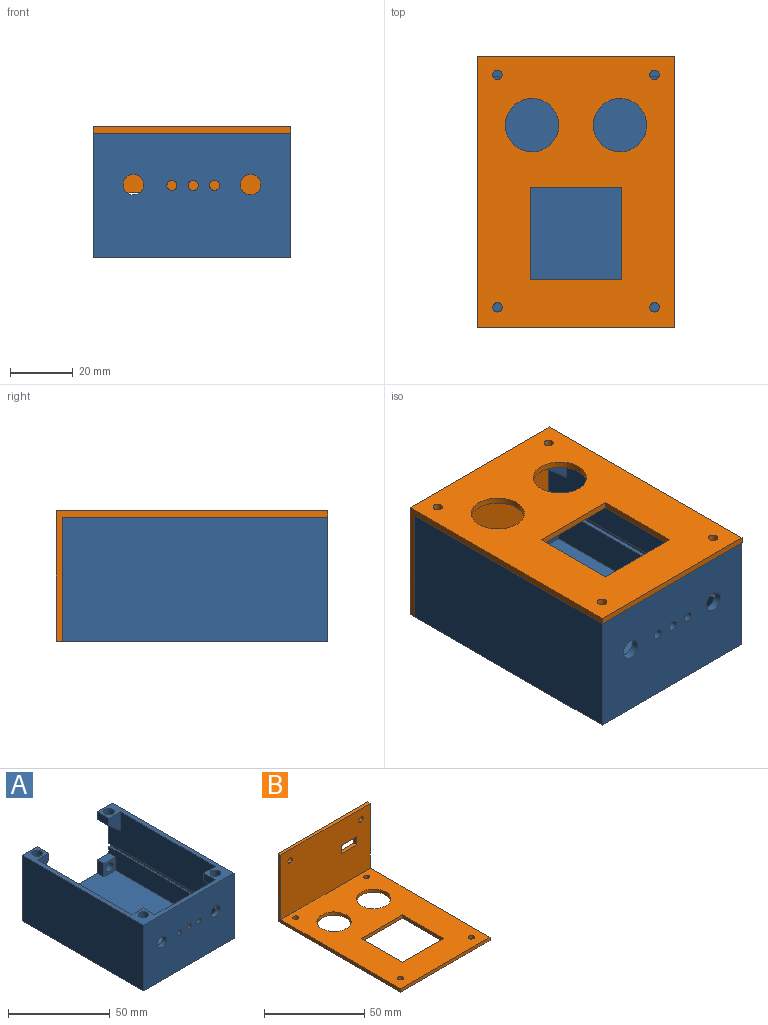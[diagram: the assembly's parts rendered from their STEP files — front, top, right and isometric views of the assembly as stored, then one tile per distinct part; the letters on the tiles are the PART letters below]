
ASSEMBLY  parts=2 mates=1
PART A: 47 faces, bbox 64x85.5x40.5 mm
  f0: plane 60x37mm, normal (0,1,0), area 1931.5mm2, adj f1,f2,f3,f4,f8,f9,f10,f11
  f1: plane 82x23mm, normal (-1,0,0), area 1702mm2, adj f0,f8,f9,f16,f34,f40,f44,f45
  f2: plane 82x23mm, normal (1,0,0), area 1702mm2, adj f0,f4,f8,f16,f32,f37,f43,f46
  f3: plane 82x58mm, normal (0,0,1), area 4684mm2, adj f0,f12,f13,f16,f17,f20,f21,f24
  f4: plane 82x1mm, normal (0,0,-1), area 82mm2, adj f0,f2,f15,f16
  f5: plane 84.5x39.5mm, normal (-1,0,0), area 3337.8mm2, adj f6,f8,f16,f30
  f6: plane 84.5x63mm, normal (0,0,-1), area 5323.5mm2, adj f5,f7,f16,f30
  f7: plane 84.5x39.5mm, normal (1,0,0), area 3337.8mm2, adj f6,f8,f16,f30
  f8: plane 84.5x63mm, normal (0,0,1), area 738.6mm2, adj f0,f1,f2,f5,f7,f16,f30,f31
  f9: plane 82x1mm, normal (0,0,-1), area 82mm2, adj f0,f1,f10,f16
  f10: plane 82x2mm, normal (-1,0,0), area 164mm2, adj f0,f9,f11,f16
  f11: plane 82x1mm, normal (0,0,1), area 82mm2, adj f0,f10,f12,f16
  f12: plane 82x12mm, normal (-1,0,0), area 948mm2, adj f0,f3,f11,f16,f19,f20
  f13: plane 82x12mm, normal (1,0,0), area 948mm2, adj f0,f3,f14,f16,f22,f24
  f14: plane 82x1mm, normal (0,0,1), area 82mm2, adj f0,f13,f15,f16
  f15: plane 82x2mm, normal (1,0,0), area 164mm2, adj f0,f4,f14,f16
  f16: plane 63x39.5mm, normal (0,1,0), area 552mm2, adj f1,f2,f3,f4,f5,f6,f7,f8
  f17: plane 8x4.5mm, normal (-1,0,0), area 36mm2, adj f3,f16,f19,f20
  f18: cylinder r=2.6mm len=5.2mm, axis (0,1,0), area 73.5mm2, adj f16,f20
  f19: plane 8x4.5mm, normal (0,0,1), area 36mm2, adj f12,f16,f17,f20
  f20: plane 8x8mm, normal (0,-1,0), area 42.8mm2, adj f3,f12,f17,f18,f19
  f21: plane 8x4.5mm, normal (1,0,0), area 36mm2, adj f3,f16,f22,f24
  f22: plane 8x4.5mm, normal (0,0,1), area 36mm2, adj f13,f16,f21,f24
  f23: cylinder r=2.6mm len=5.2mm, axis (0,1,0), area 73.5mm2, adj f16,f24
  f24: plane 8x8mm, normal (0,-1,0), area 42.8mm2, adj f3,f13,f21,f22,f23
  f25: cylinder r=3.25mm len=6.5mm, axis (0,1,0), area 51.1mm2, adj f0,f30
  f26: cylinder r=1.6mm len=3.2mm, axis (0,1,0), area 25.1mm2, adj f0,f30
  f27: cylinder r=1.6mm len=3.2mm, axis (0,1,0), area 25.1mm2, adj f0,f30
  f28: cylinder r=1.6mm len=3.2mm, axis (0,1,0), area 25.1mm2, adj f0,f30
  f29: cylinder r=3.25mm len=6.5mm, axis (0,1,0), area 51.1mm2, adj f0,f30
  f30: plane 63x39.5mm, normal (0,-1,0), area 2398mm2, adj f5,f6,f7,f8,f25,f26,f27,f28
  f31: plane 8x4.5mm, normal (1,0,0), area 36mm2, adj f0,f8,f32,f46
  f32: plane 11.5x8mm, normal (0,1,0), area 64mm2, adj f2,f8,f31,f46
  f33: cylinder r=2.6mm len=10.31mm, axis (0,0,1), area 130.7mm2, adj f8,f46
  f34: plane 11.5x8mm, normal (0,1,0), area 64mm2, adj f1,f8,f35,f45
  f35: plane 8x4.5mm, normal (-1,0,0), area 36mm2, adj f0,f8,f34,f45
  f36: cylinder r=2.6mm len=10.28mm, axis (0,0,1), area 130.7mm2, adj f8,f45
  f37: plane 11.5x8mm, normal (0,-1,0), area 64mm2, adj f2,f8,f38,f43
  f38: plane 8x4.5mm, normal (1,0,0), area 36mm2, adj f8,f16,f37,f43
  f39: cylinder r=2.6mm len=10.31mm, axis (0,0,1), area 130.7mm2, adj f8,f43
  f40: plane 11.5x8mm, normal (0,-1,0), area 64mm2, adj f1,f8,f41,f44
  f41: plane 8x4.5mm, normal (-1,0,0), area 36mm2, adj f8,f16,f40,f44
  f42: cylinder r=2.6mm len=10.28mm, axis (0,0,1), area 130.7mm2, adj f8,f44
  f43: plane 8x8mm, normal (0.66,0,-0.75), area 56.8mm2, adj f2,f16,f37,f38,f39
  f44: plane 8.96x8.96mm, normal (-0.66,0,-0.75), area 56.8mm2, adj f1,f16,f40,f41,f42
  f45: plane 8.96x8.96mm, normal (-0.66,0,-0.75), area 56.8mm2, adj f0,f1,f34,f35,f36
  f46: plane 8x8mm, normal (0.66,0,-0.75), area 56.8mm2, adj f0,f2,f31,f32,f33
PART B: 24 faces, bbox 63x86.5x41.5 mm
  f0: plane 63x39.5mm, normal (0,-1,0), area 2419.4mm2, adj f2,f3,f15,f17,f18,f19,f20,f21
  f1: plane 63x41.5mm, normal (0,1,0), area 2545.4mm2, adj f2,f3,f16,f17,f18,f19,f20,f21
  f2: plane 86.5x41.5mm, normal (1,0,0), area 252mm2, adj f0,f1,f14,f15,f16,f17
  f3: plane 86.5x41.5mm, normal (-1,0,0), area 252mm2, adj f0,f1,f14,f15,f16,f17
  f4: plane 29x2mm, normal (-1,0,0), area 58mm2, adj f5,f7,f15,f16
  f5: plane 29x2mm, normal (0,1,0), area 58mm2, adj f4,f6,f15,f16
  f6: plane 29x2mm, normal (1,0,0), area 58mm2, adj f5,f7,f15,f16
  f7: plane 29x2mm, normal (0,-1,0), area 58mm2, adj f4,f6,f15,f16
  f8: cylinder r=1.5mm len=3mm, axis (0,0,-1), area 18.8mm2, adj f15,f16
  f9: cylinder r=1.5mm len=3mm, axis (0,0,-1), area 18.8mm2, adj f15,f16
  f10: cylinder r=8.5mm len=17mm, axis (0,0,-1), area 106.8mm2, adj f15,f16
  f11: cylinder r=8.5mm len=17mm, axis (0,0,-1), area 106.8mm2, adj f15,f16
  f12: cylinder r=1.5mm len=3mm, axis (0,0,-1), area 18.8mm2, adj f15,f16
  f13: cylinder r=1.5mm len=3mm, axis (0,0,-1), area 18.8mm2, adj f15,f16
  f14: plane 63x2mm, normal (0,-1,0), area 126mm2, adj f2,f3,f15,f16
  f15: plane 84.5x63mm, normal (0,0,1), area 4000.3mm2, adj f0,f2,f3,f4,f5,f6,f7,f8
  f16: plane 86.5x63mm, normal (0,0,-1), area 4126.3mm2, adj f1,f2,f3,f4,f5,f6,f7,f8
  f17: plane 63x2mm, normal (0,0,1), area 126mm2, adj f0,f1,f2,f3
  f18: plane 5x2mm, normal (1,0,0), area 10mm2, adj f0,f1,f19,f21
  f19: plane 11x2mm, normal (0,0,-1), area 22mm2, adj f0,f1,f18,f20
  f20: plane 5x2mm, normal (-1,0,0), area 10mm2, adj f0,f1,f19,f21
  f21: plane 11x2mm, normal (0,0,1), area 22mm2, adj f0,f1,f18,f20
  f22: cylinder r=1.5mm len=3mm, axis (0,1,0), area 18.8mm2, adj f0,f1
  f23: cylinder r=1.5mm len=3mm, axis (0,1,0), area 18.8mm2, adj f0,f1
PLACE A at identity
PLACE B rot(axis=(0,1,0),180deg) t=(0,42,37.5)mm
MATE fastened B.f13 <-> A.f36  axis (0,0,-1) through (25,4,35.5)mm
